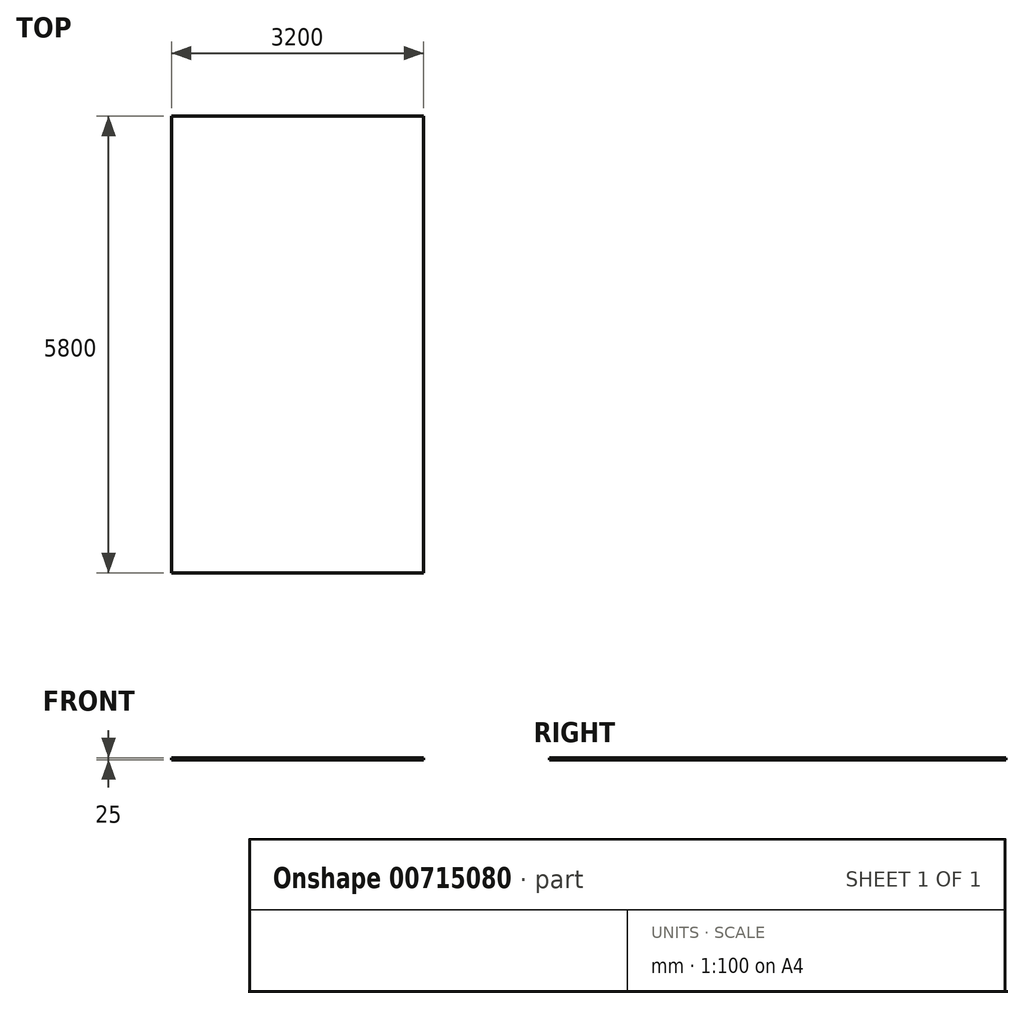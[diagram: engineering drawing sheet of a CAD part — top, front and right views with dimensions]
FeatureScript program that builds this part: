
annotation { "Feature Type Name" : "Feature", "Feature Type Description" : "" }
export const myFeature = defineFeature(function(context is Context, id is Id, definition is map)
    precondition{}
    {
        {
            var Q0;
            Q0=qCreatedBy(makeId("Top.planeOp"),FACE);
            var sketch = newSketch(context, id + "F0", { "sketchPlane" : qUnion([Q0])});
            skLineSegment(sketch, "E0.bottom", {"start": v(1600, 2900) * mm, "end": v(-1600, 2900) * mm});
            skLineSegment(sketch, "E0.top", {"start": v(1600, -2900) * mm, "end": v(-1600, -2900) * mm});
            skLineSegment(sketch, "E0.left", {"start": v(1600, 2900) * mm, "end": v(1600, -2900) * mm});
            skLineSegment(sketch, "E0.right", {"start": v(-1600, 2900) * mm, "end": v(-1600, -2900) * mm});
            skPoint(sketch, "E0.middle", {"position": v(0, 0) * mm});
            skSolve(sketch);
        }
        {
            var Q0;
            Q0=makeQuery(id+"F0.imprint","IMPRINT",FACE,{"disambiguationData":[TD([[makeQuery(id+"F0.imprint","IMPRINT",EDGE,{"derivedFrom":sQuery(id+"F0.wireOp",EDGE,"E0.bottom")}),1.0]])]});
            extrude(context, id + "F1", {"entities" : qUnion([Q0]), "endBound" : BoundingType.SYMMETRIC, "depth" : 25 * mm, "offsetDistance" : 25 * mm});
        }
    });
